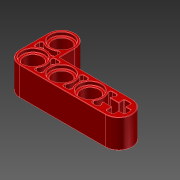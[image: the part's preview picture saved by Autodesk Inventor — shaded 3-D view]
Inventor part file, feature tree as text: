
AUTODESK INVENTOR PART (.ipt)
format: ipt  version: unknown  size: 797,184 bytes
history: native  units: mm
features: sketch x8, extrude x7, hole x1, mirror x1, fillet x1
ambient origin geometry x8: Origin, YZ Plane, XZ Plane, XY Plane, X Axis, Y Axis, Z Axis, Center Point
bodies: Volumenkörper1 (feature_tree)
feature tree (18):
  extrude  "Extrusion1"  Depth=15.4mm
  extrude  "Extrusion2"  Depth=7.4mm
  extrude  "Extrusion4"  Depth=8.0mm TaperAngle=0.0deg
  extrude  "Extrusion5"  Depth=6.2mm
  hole  "Bohrung1"  [1 undecoded]
  extrude  "Extrusion6"  Depth=1.9mm
  extrude  "Extrusion7"  Depth=1.9mm
  extrude  "Extrusion8"  Depth=1.9mm
  mirror  "Spiegeln1"
  fillet  "Rundung1"  Radius=0.95mm
  sketch  "Skizze1"  dims[d0=31.4mm d1=15.4mm]
  sketch  "Skizze2"  dims[d2=8.0mm d3=0.0mm d4=7.4mm]
  sketch  "Skizze3"  dims[d5=7.4mm d6=8.0mm d7=0.0mm]
  sketch  "Skizze4"  dims[d10=8.0mm d11=0.0mm d12=6.2mm]
  sketch  "Skizze5"  dims[d13=8.0mm d14=8.0mm]
  sketch  "Skizze6"  dims[d15=1.0mm d16=0.0mm]
  sketch  "Skizze7"  dims[d17=4.9mm d18=6.0mm d19=6.2mm d20=1.0mm d21=90.0deg d22=8.0mm d23=20.594885mm d24=1.9mm]
  sketch  "Skizze8"  dims[d25=1.9mm d26=1.9mm d28=1.9mm d29=0.95mm d30=0.95mm d31=0.95mm d32=0.95mm d33=5.0mm d34=2.5mm d35=5.0mm d36=2.5mm d37=1.0mm d38=0.0mm d39=0.1mm d40=0.1mm d41=0.1mm d42=0.1mm d43=7.25mm d44=7.25mm d45=5.5mm d46=2.75mm d47=0.5mm d48=1.0mm d49=0.0mm d50=3.625mm d51=3.625mm d52=1.085342mm d54=7.25mm d55=5.5mm d56=2.75mm d57=3.625mm d58=0.5mm d59=7.25mm d60=5.5mm d61=3.625mm d62=0.5mm d63=7.25mm d64=5.5mm d65=3.625mm d66=0.5mm d69=1.5mm d70=0.0mm d71=0.1mm d72=0.1mm]
note: 1 required parameter value undecoded (feature->parameter linkage not recoverable at this tier; creation-order binding heuristic only, values carry confidence <= 0.55)
